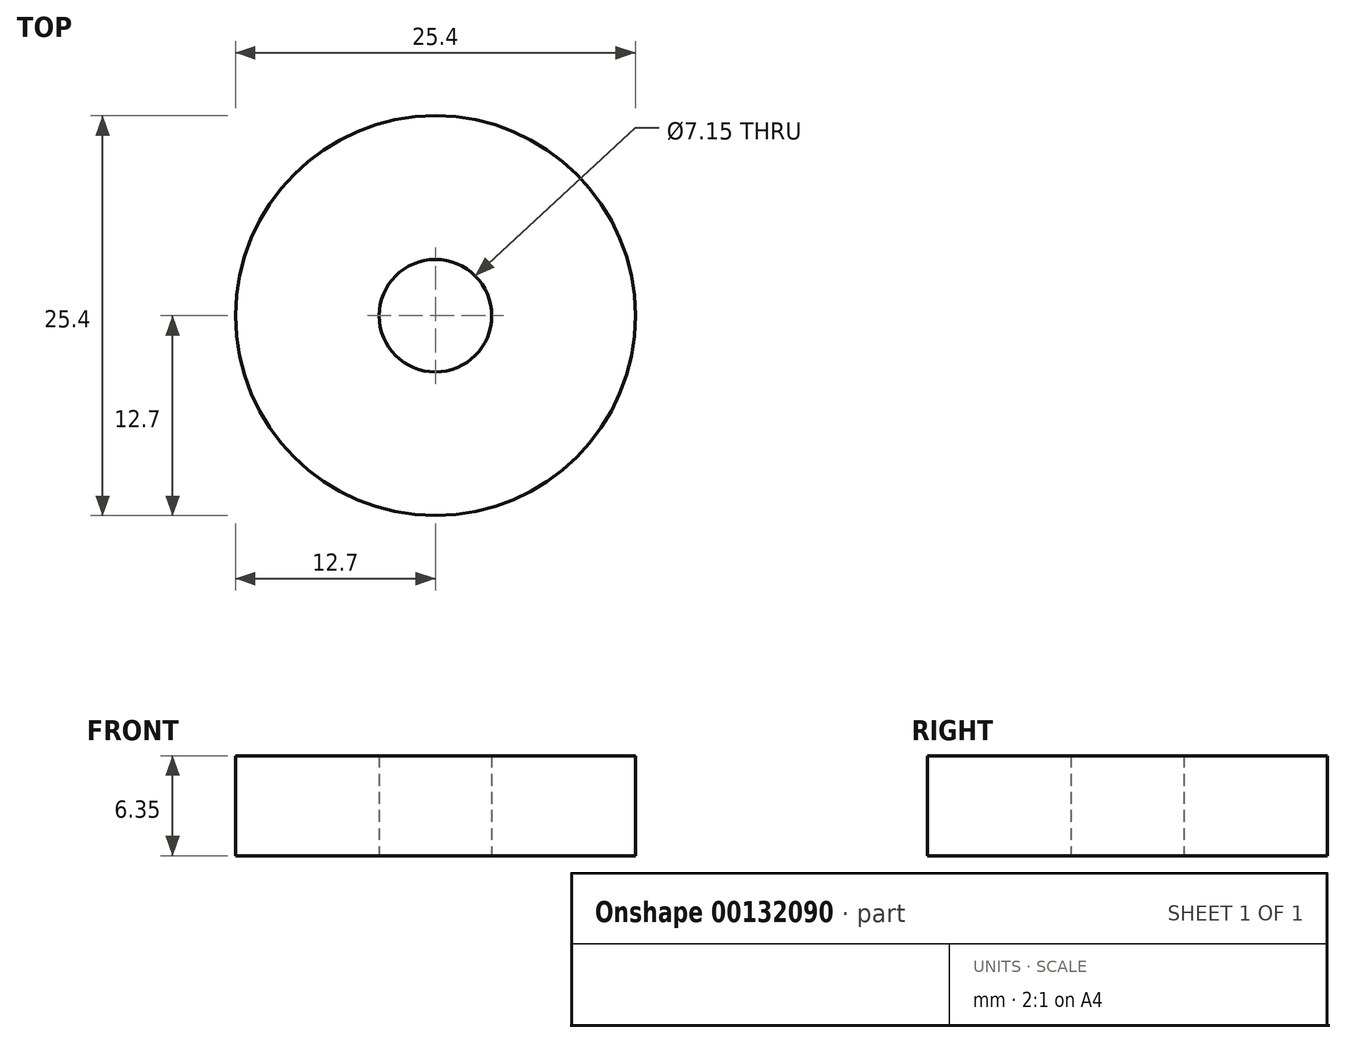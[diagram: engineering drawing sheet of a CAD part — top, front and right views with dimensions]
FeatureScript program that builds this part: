
annotation { "Feature Type Name" : "Feature", "Feature Type Description" : "" }
export const myFeature = defineFeature(function(context is Context, id is Id, definition is map)
    precondition{}
    {
        {
            var Q0;
            Q0=qCreatedBy(makeId("Top.planeOp"),FACE);
            var sketch = newSketch(context, id + "F0", { "sketchPlane" : qUnion([Q0])});
            skCircle(sketch, "E0", {"center": v(0, 0) * mm, "radius": 12.7 * mm});
            skCircle(sketch, "E1", {"center": v(0, 0) * mm, "radius": 3.58 * mm});
            skSolve(sketch);
        }
        {
            var Q0;
            Q0=makeQuery(id+"F0.imprint","IMPRINT",FACE,{"disambiguationData":[TD([[makeQuery(id+"F0.imprint","IMPRINT",EDGE,{"derivedFrom":sQuery(id+"F0.wireOp",EDGE,"E0")}),1.0]])]});
            extrude(context, id + "F1", {"entities" : qUnion([Q0]), "depth" : 6.35 * mm});
        }
    });
